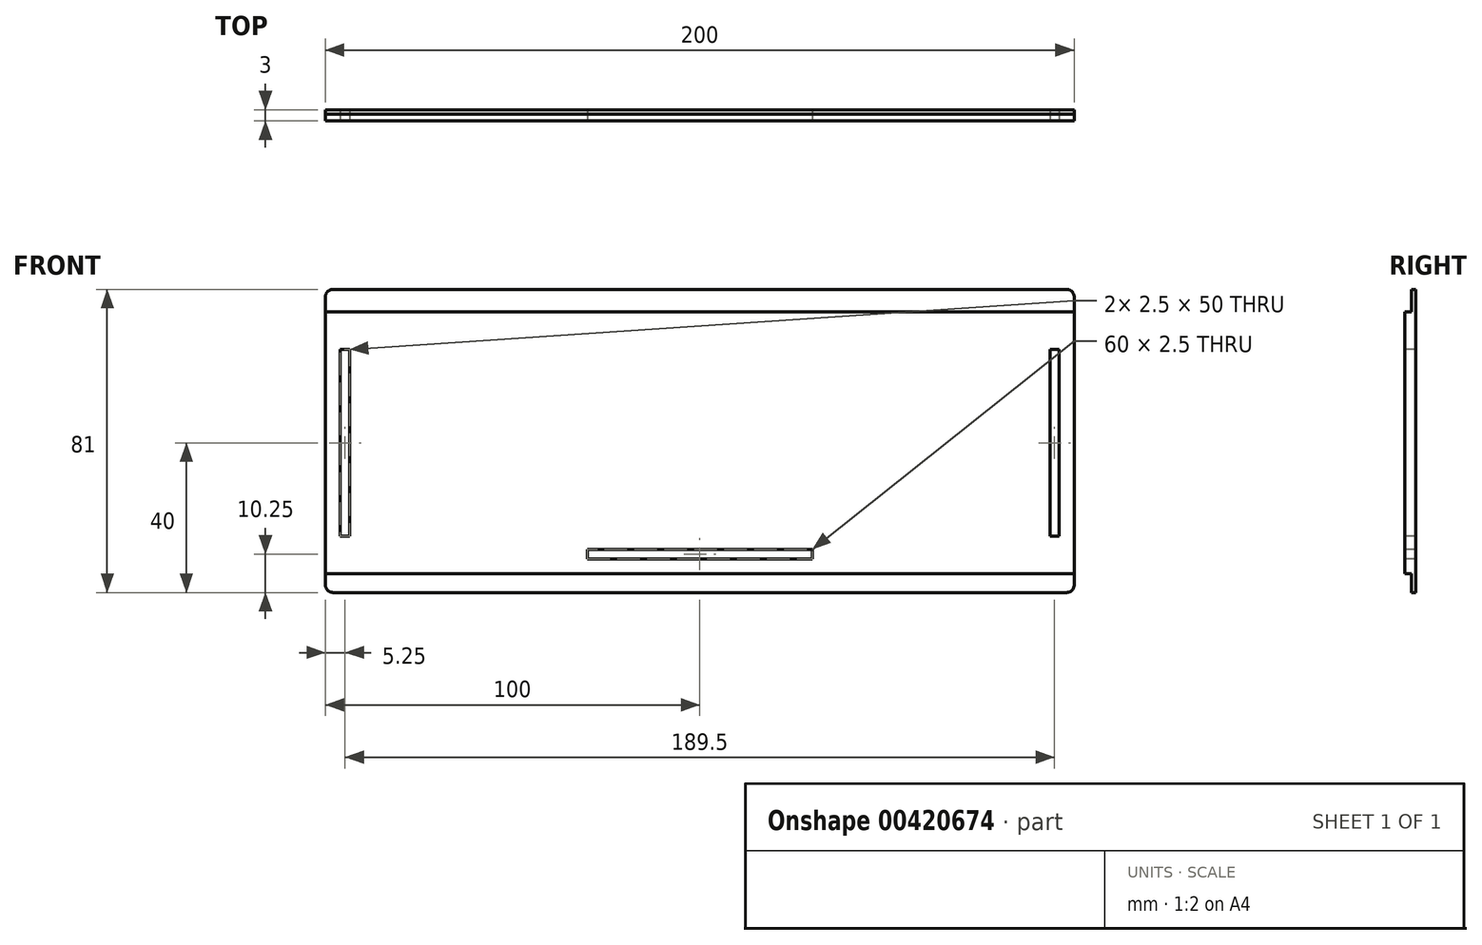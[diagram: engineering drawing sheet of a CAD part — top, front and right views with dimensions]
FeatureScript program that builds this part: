
annotation { "Feature Type Name" : "Feature", "Feature Type Description" : "" }
export const myFeature = defineFeature(function(context is Context, id is Id, definition is map)
    precondition{}
    {
        {
            var Q0;
            Q0=qCreatedBy(makeId("Front.planeOp"),FACE);
            var sketch = newSketch(context, id + "F0", { "sketchPlane" : qUnion([Q0])});
            skLineSegment(sketch, "E0.bottom", {"start": v(100, -40.5) * mm, "end": v(-100, -40.5) * mm});
            skLineSegment(sketch, "E0.top", {"start": v(100, 40.5) * mm, "end": v(-100, 40.5) * mm});
            skLineSegment(sketch, "E0.left", {"start": v(100, -40.5) * mm, "end": v(100, 40.5) * mm});
            skLineSegment(sketch, "E0.right", {"start": v(-100, -40.5) * mm, "end": v(-100, 40.5) * mm});
            skPoint(sketch, "E0.middle", {"position": v(0, 0) * mm});
            skSolve(sketch);
        }
        {
            var Q0;
            Q0=qSketchRegion(id+"F0",true);
            extrude(context, id + "F1", {"entities" : qUnion([Q0]), "depth" : 3 * mm});
        }
        {
            var Q0;
            Q0=makeQuery(id+"F1.opExtrude","CAP_FACE",FACE,{"disambiguationData":[OSD([sQuery(id+"F0.wireOp",EDGE,"E0.bottom"),sQuery(id+"F0.wireOp",EDGE,"E0.top"),sQuery(id+"F0.wireOp",EDGE,"E0.left"),sQuery(id+"F0.wireOp",EDGE,"E0.right")])],"isStart":false});
            var sketch = newSketch(context, id + "F2", { "sketchPlane" : qUnion([Q0])});
            skLineSegment(sketch, "E1", {"start": v(-100, 40.5) * mm, "end": v(100, 40.5) * mm});
            skLineSegment(sketch, "E2", {"start": v(100, 40.5) * mm, "end": v(100, 34.5) * mm});
            skLineSegment(sketch, "E3", {"start": v(100, 34.5) * mm, "end": v(-100, 34.5) * mm});
            skLineSegment(sketch, "E4", {"start": v(-100, 34.5) * mm, "end": v(-100, 40.5) * mm});
            skLineSegment(sketch, "E5", {"start": v(-100, -40.5) * mm, "end": v(100, -40.5) * mm});
            skLineSegment(sketch, "E6", {"start": v(100, -40.5) * mm, "end": v(100, -35.5) * mm});
            skLineSegment(sketch, "E7", {"start": v(100, -35.5) * mm, "end": v(-100, -35.5) * mm});
            skLineSegment(sketch, "E8", {"start": v(-100, -35.5) * mm, "end": v(-100, -40.5) * mm});
            skSolve(sketch);
        }
        {
            var Q0;
            Q0=qSketchRegion(id+"F2",true);
            extrude(context, id + "F3", {"entities" : qUnion([Q0]), "operationType" : NewBodyOperationType.REMOVE, "oppositeDirection" : true, "depth" : 1.8 * mm});
        }
        {
            var Q0;
            Q0=makeQuery(id+"F1.opExtrude","SWEPT_EDGE",EDGE,{"disambiguationData":[OSD([sQuery(id+"F0.wireOp",EDGE,"E0.bottom"),sQuery(id+"F0.wireOp",EDGE,"E0.right")])]});
            var Q1;
            Q1=makeQuery(id+"F1.opExtrude","SWEPT_EDGE",EDGE,{"disambiguationData":[OSD([sQuery(id+"F0.wireOp",EDGE,"E0.top"),sQuery(id+"F0.wireOp",EDGE,"E0.right")])]});
            var Q2;
            Q2=makeQuery(id+"F1.opExtrude","SWEPT_EDGE",EDGE,{"disambiguationData":[OSD([sQuery(id+"F0.wireOp",EDGE,"E0.bottom"),sQuery(id+"F0.wireOp",EDGE,"E0.left")])]});
            var Q3;
            Q3=makeQuery(id+"F1.opExtrude","SWEPT_EDGE",EDGE,{"disambiguationData":[OSD([sQuery(id+"F0.wireOp",EDGE,"E0.top"),sQuery(id+"F0.wireOp",EDGE,"E0.left")])]});
            fillet(context, id + "F4", {"entities" : qUnion([Q0, Q1, Q2, Q3]), "radius" : 2 * mm, "tangentPropagation" : true, "allowEdgeOverflow" : false});
        }
        {
            var Q0;
            Q0=makeQuery(id+"F1.opExtrude","CAP_FACE",FACE,{"disambiguationData":[OSD([sQuery(id+"F0.wireOp",EDGE,"E0.bottom"),sQuery(id+"F0.wireOp",EDGE,"E0.top"),sQuery(id+"F0.wireOp",EDGE,"E0.left"),sQuery(id+"F0.wireOp",EDGE,"E0.right")])],"isStart":false});
            var sketch = newSketch(context, id + "F5", { "sketchPlane" : qUnion([Q0])});
            skLineSegment(sketch, "E9", {"start": v(-96, 24.5) * mm, "end": v(-96, -25.5) * mm});
            skLineSegment(sketch, "E10", {"start": v(-96, -25.5) * mm, "end": v(-93.5, -25.5) * mm});
            skLineSegment(sketch, "E11", {"start": v(-93.5, -25.5) * mm, "end": v(-93.5, 24.5) * mm});
            skLineSegment(sketch, "E12", {"start": v(-93.5, 24.5) * mm, "end": v(-96, 24.5) * mm});
            skLineSegment(sketch, "E13.MirrorCS", {"start": v(93.5, -25.5) * mm, "end": v(93.5, 24.5) * mm});
            skLineSegment(sketch, "E14.MirrorCS", {"start": v(96, 24.5) * mm, "end": v(96, -25.5) * mm});
            skLineSegment(sketch, "E15.MirrorCS", {"start": v(93.5, 24.5) * mm, "end": v(96, 24.5) * mm});
            skLineSegment(sketch, "E16.MirrorCS", {"start": v(96, -25.5) * mm, "end": v(93.5, -25.5) * mm});
            skLineSegment(sketch, "E17.bottom", {"start": v(30, -31.5) * mm, "end": v(-30, -31.5) * mm});
            skLineSegment(sketch, "E17.top", {"start": v(30, -29) * mm, "end": v(-30, -29) * mm});
            skLineSegment(sketch, "E17.left", {"start": v(30, -31.5) * mm, "end": v(30, -29) * mm});
            skLineSegment(sketch, "E17.right", {"start": v(-30, -31.5) * mm, "end": v(-30, -29) * mm});
            skPoint(sketch, "E17.middle", {"position": v(0, -30.25) * mm});
            skSolve(sketch);
        }
        {
            var Q0;
            Q0=qSketchRegion(id+"F5",true);
            extrude(context, id + "F6", {"entities" : qUnion([Q0]), "operationType" : NewBodyOperationType.REMOVE, "oppositeDirection" : true, "depth" : 25 * mm});
        }
    });
